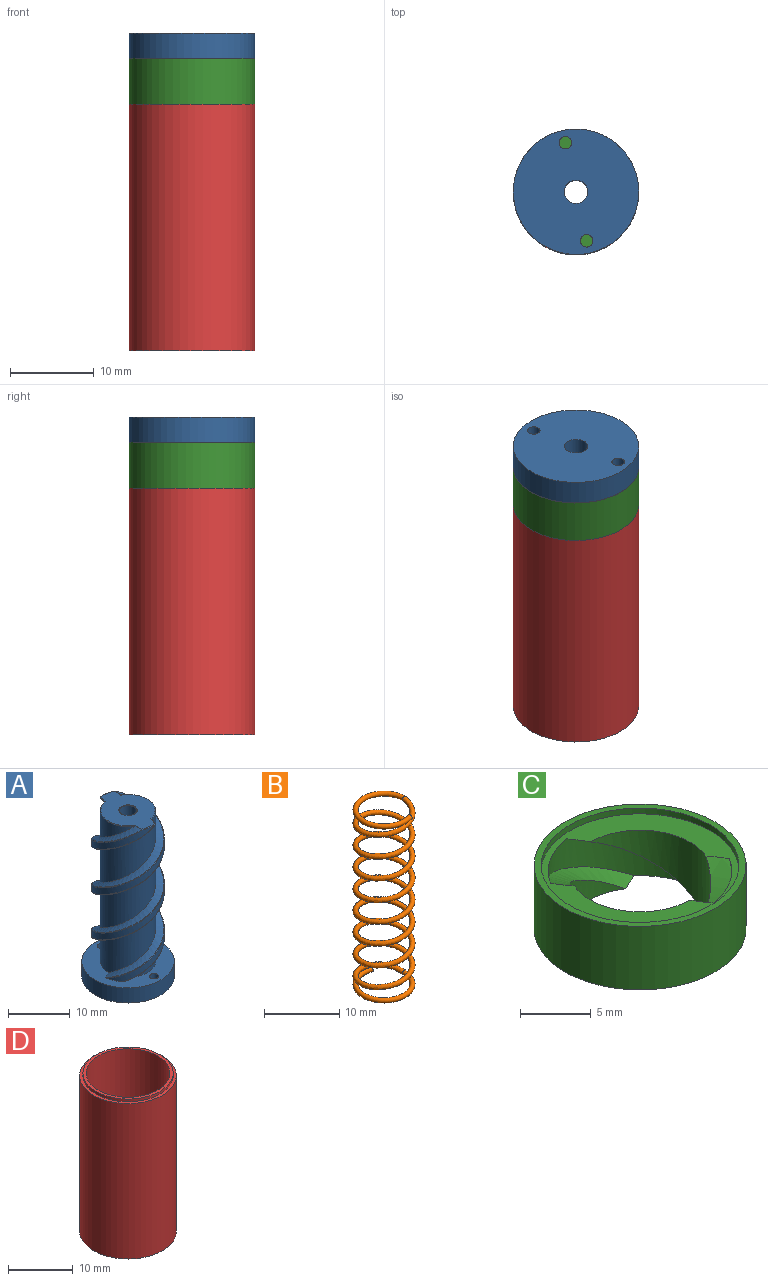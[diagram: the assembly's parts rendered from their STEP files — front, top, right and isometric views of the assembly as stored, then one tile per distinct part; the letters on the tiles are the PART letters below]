
ASSEMBLY  parts=4 mates=3
PART A: 32 faces, bbox 15x15x34.4 mm
  f0: bspline ~32.79x12.4mm, area 84mm2, adj f7,f9,f25,f28,f29
  f1: bspline ~32.78x12.4mm, area 83.5mm2, adj f6,f9,f18,f19
  f2: cylinder r=5.9mm len=29.9mm, axis (0,0,-1), area 81.4mm2, adj f9,f19,f24,f25
  f3: bspline ~32.79x12.4mm, area 84mm2, adj f6,f9,f14,f15,f16
  f4: bspline ~32.78x12.4mm, area 83.5mm2, adj f7,f9,f20,f26
  f5: cylinder r=5.9mm len=29.9mm, axis (0,0,-1), area 81.4mm2, adj f9,f14,f20,f21
  f6: cylinder r=4.5mm len=29.9mm, axis (0,0,-1), area 317mm2, adj f1,f3,f9,f16,f18
  f7: cylinder r=4.5mm len=29.9mm, axis (0,0,-1), area 317mm2, adj f0,f4,f9,f26,f28
  f8: plane 11.6x8.8mm, normal (0,0,1), area 62.1mm2, adj f13,f15,f16,f18,f21,f24,f26,f28
  f9: plane 15.03x15.03mm, normal (0,0,1), area 100.1mm2, adj f0,f1,f2,f3,f4,f5,f6,f7
  f10: plane 15x15mm, normal (0,0,-1), area 167mm2, adj f11,f12,f30,f31
  f11: cylinder r=7.5mm len=15mm, axis (0,0,1), area 141.4mm2, adj f9,f10
  f12: cylinder r=1.4mm len=32.9mm, axis (0,0,1), area 289.4mm2, adj f10,f13
  f13: torus R=1.5mm, axis (0,0,1), area 1.4mm2, adj f8,f12
  f14: bspline ~31.14x11.82mm, area 9.1mm2, adj f3,f5,f9,f17
  f15: bspline ~1.82x0.14mm, area 0.1mm2, adj f3,f8,f16,f17
  f16: torus R=4.4mm, axis (0,0,1), area 1.7mm2, adj f3,f6,f8,f15,f18
  f17: sphere r=0.1mm, area 0mm2, adj f14,f15,f21
  f18: bspline ~2.06x0.93mm, area 0.4mm2, adj f1,f6,f8,f16,f22
  f19: bspline ~30.78x11.82mm, area 9.1mm2, adj f1,f2,f9,f22
  f20: bspline ~30.78x11.82mm, area 9.1mm2, adj f4,f5,f9,f23
  f21: torus R=5.8mm, axis (0,0,1), area 0.4mm2, adj f5,f8,f17,f23
  f22: sphere r=0.1mm, area 0mm2, adj f18,f19,f24
  f23: sphere r=0.1mm, area 0mm2, adj f20,f21,f26
  f24: torus R=5.8mm, axis (0,0,1), area 0.4mm2, adj f2,f8,f22,f27
  f25: bspline ~31.14x11.82mm, area 9.1mm2, adj f0,f2,f9,f27
  f26: bspline ~2.06x0.93mm, area 0.4mm2, adj f4,f7,f8,f23,f28
  f27: sphere r=0.1mm, area 0mm2, adj f24,f25,f29
  f28: torus R=4.4mm, axis (0,0,1), area 1.7mm2, adj f0,f7,f8,f26,f29
  f29: bspline ~1.82x0.14mm, area 0.1mm2, adj f0,f8,f27,f28
  f30: cylinder r=0.75mm len=3mm, axis (0,0,-1), area 14.1mm2, adj f9,f10
  f31: cylinder r=0.75mm len=3mm, axis (0,0,-1), area 14.1mm2, adj f9,f10
PART B: 5 faces, bbox 8.9x8.9x29 mm
  f0: bspline ~29x8.24mm, area 418mm2, adj f1,f2,f3,f4
  f1: torus R=3.78mm, axis (0,0,-1), area 42mm2, adj f0,f2
  f2: plane 0.7x0.66mm, normal (0.94,0.34,0), area 0.4mm2, adj f0,f1
  f3: torus R=3.78mm, axis (0,0,1), area 42mm2, adj f0,f4
  f4: plane 0.7x0.66mm, normal (0.94,-0.34,0), area 0.4mm2, adj f0,f3
PART C: 13 faces, bbox 15x15x9 mm
  f0: cylinder r=7.5mm len=15mm, axis (0,0,-1), area 259.2mm2, adj f2,f12
  f1: plane 14.03x14.03mm, normal (0,0,1), area 57.9mm2, adj f3,f4,f5,f6,f7,f8,f9,f10
  f2: plane 15.03x15.03mm, normal (0,0,-1), area 80.6mm2, adj f0,f3,f4,f5,f6,f7,f8,f9
  f3: cylinder r=6.5mm len=12.03mm, axis (0,0,-1), area 28.7mm2, adj f1,f2,f4,f5
  f4: bspline ~10.47x8.79mm, area 17.3mm2, adj f1,f2,f3,f10
  f5: bspline ~12.36x7.74mm, area 17.3mm2, adj f1,f2,f3,f9
  f6: cylinder r=6.5mm len=12.03mm, axis (0,0,-1), area 28.7mm2, adj f1,f2,f7,f8
  f7: bspline ~10.47x8.79mm, area 17.3mm2, adj f1,f2,f6,f9
  f8: bspline ~12.36x7.74mm, area 17.3mm2, adj f1,f2,f6,f10
  f9: cylinder r=5mm len=10mm, axis (0,0,-1), area 49.4mm2, adj f1,f2,f5,f7
  f10: cylinder r=5mm len=10mm, axis (0,0,-1), area 49.4mm2, adj f1,f2,f4,f8
  f11: cylinder r=7mm len=14mm, axis (0,0,-1), area 22mm2, adj f1,f12
  f12: plane 15x15mm, normal (0,0,1), area 22.8mm2, adj f0,f11
PART D: 8 faces, bbox 15x15x30 mm
  f0: cylinder r=7.5mm len=29.5mm, axis (0,0,-1), area 1390.2mm2, adj f5,f7
  f1: plane 14x14mm, normal (0,0,1), area 21.2mm2, adj f2,f6
  f2: cylinder r=6.5mm len=27mm, axis (0,0,-1), area 1102.7mm2, adj f1,f3
  f3: plane 13x13mm, normal (0,0,1), area 120.2mm2, adj f2,f4
  f4: cylinder r=2mm len=4mm, axis (0,0,1), area 37.7mm2, adj f3,f5
  f5: plane 15x15mm, normal (0,0,-1), area 164.1mm2, adj f0,f4
  f6: cylinder r=7mm len=14mm, axis (0,0,1), area 22mm2, adj f1,f7
  f7: plane 15x15mm, normal (0,0,1), area 22.8mm2, adj f0,f6
PLACE A rot(axis=(-0.11,0.99,0),180deg) t=(6.6,9.08,27.92)mm
PLACE B rot(axis=(0,0,1),11.9deg) t=(6.6,9.08,-3.75)mm
PLACE C rot(axis=(0.99,0.1,0),180deg) t=(6.6,9.08,27.9)mm
PLACE D rot(axis=(0,0,1),11.9deg) t=(6.6,9.08,-4.1)mm fixed
MATE cylindrical C.f0 <-> A.f11  axis (0,0,1) through (6.6,9.08,27.9)mm
MATE fastened D.f0 <-> C.f0  axis (0,0,-1) through (6.6,9.08,22.4)mm
MATE fastened B.f1 <-> D.f2  axis (0,0,1) through (6.6,9.08,-3.75)mm
